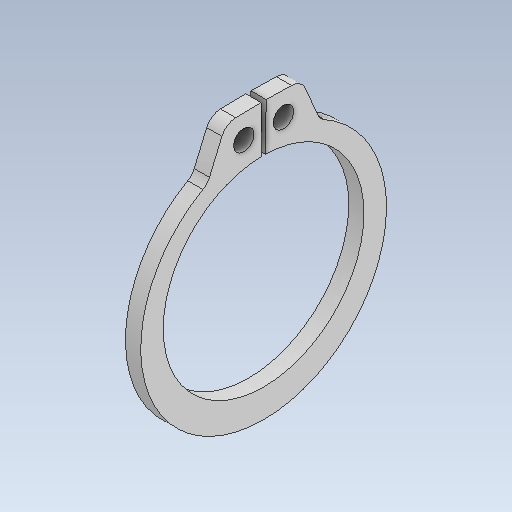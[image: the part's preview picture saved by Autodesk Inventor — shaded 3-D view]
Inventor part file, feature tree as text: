
AUTODESK INVENTOR PART (.ipt)
format: ipt  version: 2023 (Build 270158000, 158)  size: 103,424 bytes
history: native  units: in
note: dims shown in document units (in); Inventor stores cm internally (conversion verified against a paired STEP export)
features: fillet x1
ambient origin geometry x8: Origin, YZ Plane, XZ Plane, XY Plane, X Axis, Y Axis, Z Axis, Center Point
bodies: Solid1 (feature_tree)
feature tree (1):
  fillet  "Fillet1"  [1 undecoded]
note: 1 required parameter value undecoded (feature->parameter linkage not recoverable at this tier; creation-order binding heuristic only, values carry confidence <= 0.55)
